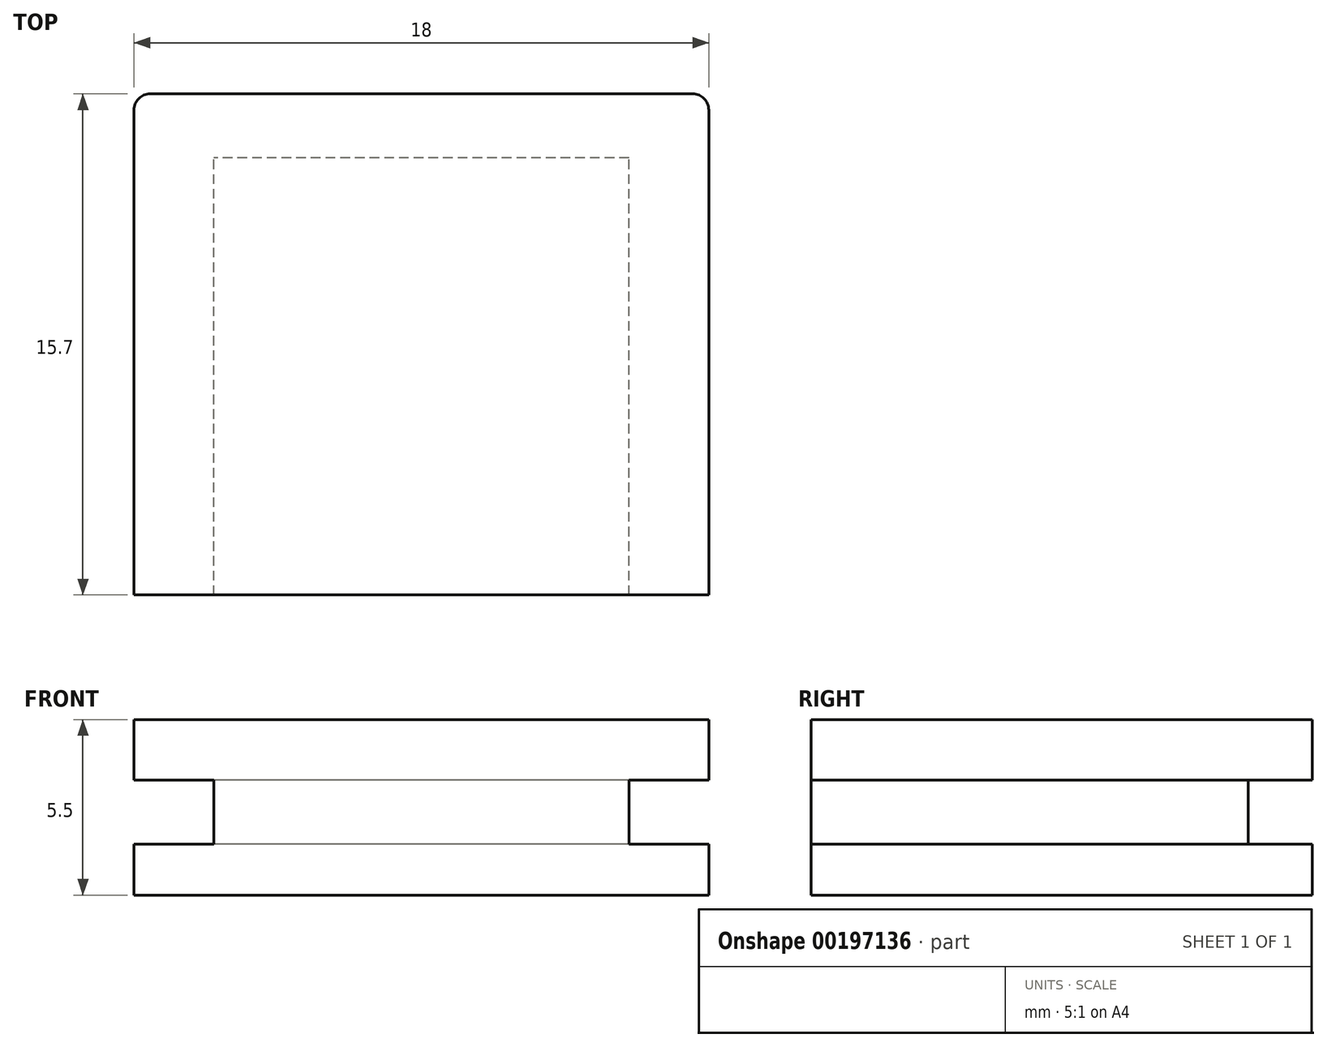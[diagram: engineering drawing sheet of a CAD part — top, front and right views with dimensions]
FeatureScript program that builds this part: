
annotation { "Feature Type Name" : "Feature", "Feature Type Description" : "" }
export const myFeature = defineFeature(function(context is Context, id is Id, definition is map)
    precondition{}
    {
        {
            var Q0;
            Q0=qCreatedBy(makeId("Top.planeOp"),FACE);
            var sketch = newSketch(context, id + "F0", { "sketchPlane" : qUnion([Q0])});
            skLineSegment(sketch, "E0.bottom", {"start": v(-9, 7.85) * mm, "end": v(9, 7.85) * mm});
            skLineSegment(sketch, "E0.top", {"start": v(-9, -7.85) * mm, "end": v(9, -7.85) * mm});
            skLineSegment(sketch, "E0.left", {"start": v(-9, 7.85) * mm, "end": v(-9, -7.85) * mm});
            skLineSegment(sketch, "E0.right", {"start": v(9, 7.85) * mm, "end": v(9, -7.85) * mm});
            skPoint(sketch, "E0.middle", {"position": v(0, 0) * mm});
            skSolve(sketch);
        }
        {
            var Q0;
            Q0 = qSketchRegion(id + "F0", true);
            extrude(context, id + "F1", {"entities" : qUnion([Q0]), "oppositeDirection" : true, "depth" : 5.5 * mm});
        }
        {
            var Q0;
            Q0=makeQuery(id+"F1.opExtrude","SWEPT_EDGE",EDGE,{"disambiguationData":[OSD([sQuery(id+"F0.wireOp",EDGE,"E0.bottom"),sQuery(id+"F0.wireOp",EDGE,"E0.right")])]});
            var Q1;
            Q1=makeQuery(id+"F1.opExtrude","SWEPT_EDGE",EDGE,{"disambiguationData":[OSD([sQuery(id+"F0.wireOp",EDGE,"E0.bottom"),sQuery(id+"F0.wireOp",EDGE,"E0.left")])]});
            fillet(context, id + "F2", {"entities" : qUnion([Q0, Q1]), "radius" : 0.5 * mm, "tangentPropagation" : true, "allowEdgeOverflow" : false});
        }
        {
            var Q0;
            Q0=makeQuery(id+"F1.opExtrude","SWEPT_FACE",FACE,{"disambiguationData":[OSD([sQuery(id+"F0.wireOp",EDGE,"E0.bottom")])]});
            var sketch = newSketch(context, id + "F3", { "sketchPlane" : qUnion([Q0])});
            skLineSegment(sketch, "E1.0", {"start": v(-9, -5.5) * mm, "end": v(-9, 0) * mm});
            skLineSegment(sketch, "E1.1", {"start": v(9, 0) * mm, "end": v(9, -5.5) * mm});
            skLineSegment(sketch, "E2", {"start": v(-9, -3.9) * mm, "end": v(9, -3.9) * mm});
            skLineSegment(sketch, "E3", {"start": v(-9, -1.9) * mm, "end": v(9, -1.9) * mm});
            skLineSegment(sketch, "E4", {"start": v(-6.5, -1.9) * mm, "end": v(-6.5, -3.9) * mm});
            skLineSegment(sketch, "E5", {"start": v(0, 0) * mm, "end": v(0, -5.5) * mm, "construction": true});
            skLineSegment(sketch, "E6.MirrorCS", {"start": v(6.5, -1.9) * mm, "end": v(6.5, -3.9) * mm});
            skSolve(sketch);
        }
        {
            var Q0;
            {var subQ0=sQuery(id+"F3.wireOp",EDGE,"E4");Q0=makeQuery(id+"F3.imprint","IMPRINT",FACE,{"disambiguationData":[TD([[makeQuery(id+"F3.imprint","IMPRINT",EDGE,{"derivedFrom":subQ0}),-1.0]])]});}
            var Q1;
            {var subQ0=sQuery(id+"F3.wireOp",EDGE,"E2");var subQ1=sQuery(id+"F3.wireOp",EDGE,"E1.0");var subQ2=makeQuery(id+"F3.imprint","INTERSECT",VERTEX,{"derivedFrom":[subQ1,subQ0]});Q1=makeQuery(id+"F3.imprint","IMPRINT",FACE,{"disambiguationData":[TD([[makeQuery(id+"F3.imprint","IMPRINT",EDGE,{"disambiguationData":[TD([[subQ2,-1.0]])],"derivedFrom":subQ1}),-1.0]])]});}
            var Q2;
            {var subQ0=sQuery(id+"F3.wireOp",EDGE,"E6.MirrorCS");Q2=makeQuery(id+"F3.imprint","IMPRINT",FACE,{"disambiguationData":[TD([[makeQuery(id+"F3.imprint","IMPRINT",EDGE,{"derivedFrom":subQ0}),1.0]])]});}
            var Q3;
            {var subQ0=sQuery(id+"F3.wireOp",EDGE,"E2");var subQ1=sQuery(id+"F3.wireOp",EDGE,"E1.1");var subQ2=makeQuery(id+"F3.imprint","INTERSECT",VERTEX,{"derivedFrom":[subQ1,subQ0]});Q3=makeQuery(id+"F3.imprint","IMPRINT",FACE,{"disambiguationData":[TD([[makeQuery(id+"F3.imprint","IMPRINT",EDGE,{"disambiguationData":[TD([[subQ2,1.0]])],"derivedFrom":subQ1}),-1.0]])]});}
            extrude(context, id + "F4", {"entities" : qUnion([Q0, Q1, Q2, Q3]), "operationType" : NewBodyOperationType.REMOVE, "oppositeDirection" : true, "depth" : 25 * mm});
        }
        {
            var Q0;
            {var subQ0=sQuery(id+"F3.wireOp",EDGE,"E4");Q0=makeQuery(id+"F3.imprint","IMPRINT",FACE,{"disambiguationData":[TD([[makeQuery(id+"F3.imprint","IMPRINT",EDGE,{"derivedFrom":subQ0}),1.0]])]});}
            extrude(context, id + "F5", {"entities" : qUnion([Q0]), "operationType" : NewBodyOperationType.REMOVE, "oppositeDirection" : true, "depth" : 2 * mm});
        }
    });
